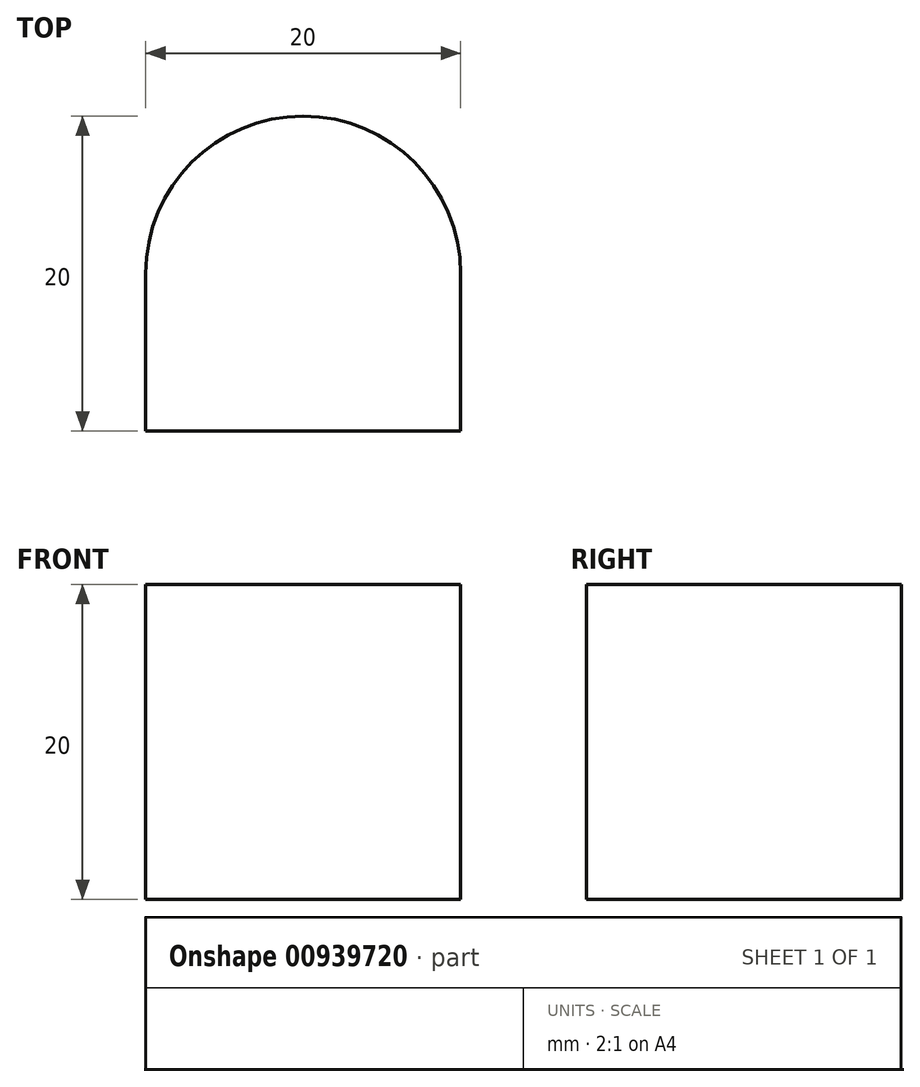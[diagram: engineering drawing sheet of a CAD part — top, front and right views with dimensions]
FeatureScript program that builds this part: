
annotation { "Feature Type Name" : "Feature", "Feature Type Description" : "" }
export const myFeature = defineFeature(function(context is Context, id is Id, definition is map)
    precondition{}
    {
        {
            var Q0;
            Q0=qCreatedBy(makeId("Top.planeOp"),FACE);
            var sketch = newSketch(context, id + "F0", { "sketchPlane" : qUnion([Q0])});
            skArc(sketch, "E0", {"start": v(20, 0) * mm, "mid": v(10, 10) * mm, "end": v(0, 0) * mm});
            skLineSegment(sketch, "E1", {"start": v(0, 0) * mm, "end": v(0, -10) * mm});
            skLineSegment(sketch, "E2", {"start": v(0, -10) * mm, "end": v(20, -10) * mm});
            skLineSegment(sketch, "E3", {"start": v(20, -10) * mm, "end": v(20, 0) * mm});
            skSolve(sketch);
        }
        {
            var Q0;
            Q0=makeQuery(id+"F0.imprint","IMPRINT",FACE,{"disambiguationData":[TD([[makeQuery(id+"F0.imprint","IMPRINT",EDGE,{"derivedFrom":sQuery(id+"F0.wireOp",EDGE,"E0")}),1.0]])]});
            extrude(context, id + "F1", {"entities" : qUnion([Q0]), "depth" : 20 * mm, "offsetDistance" : 25 * mm});
        }
    });
